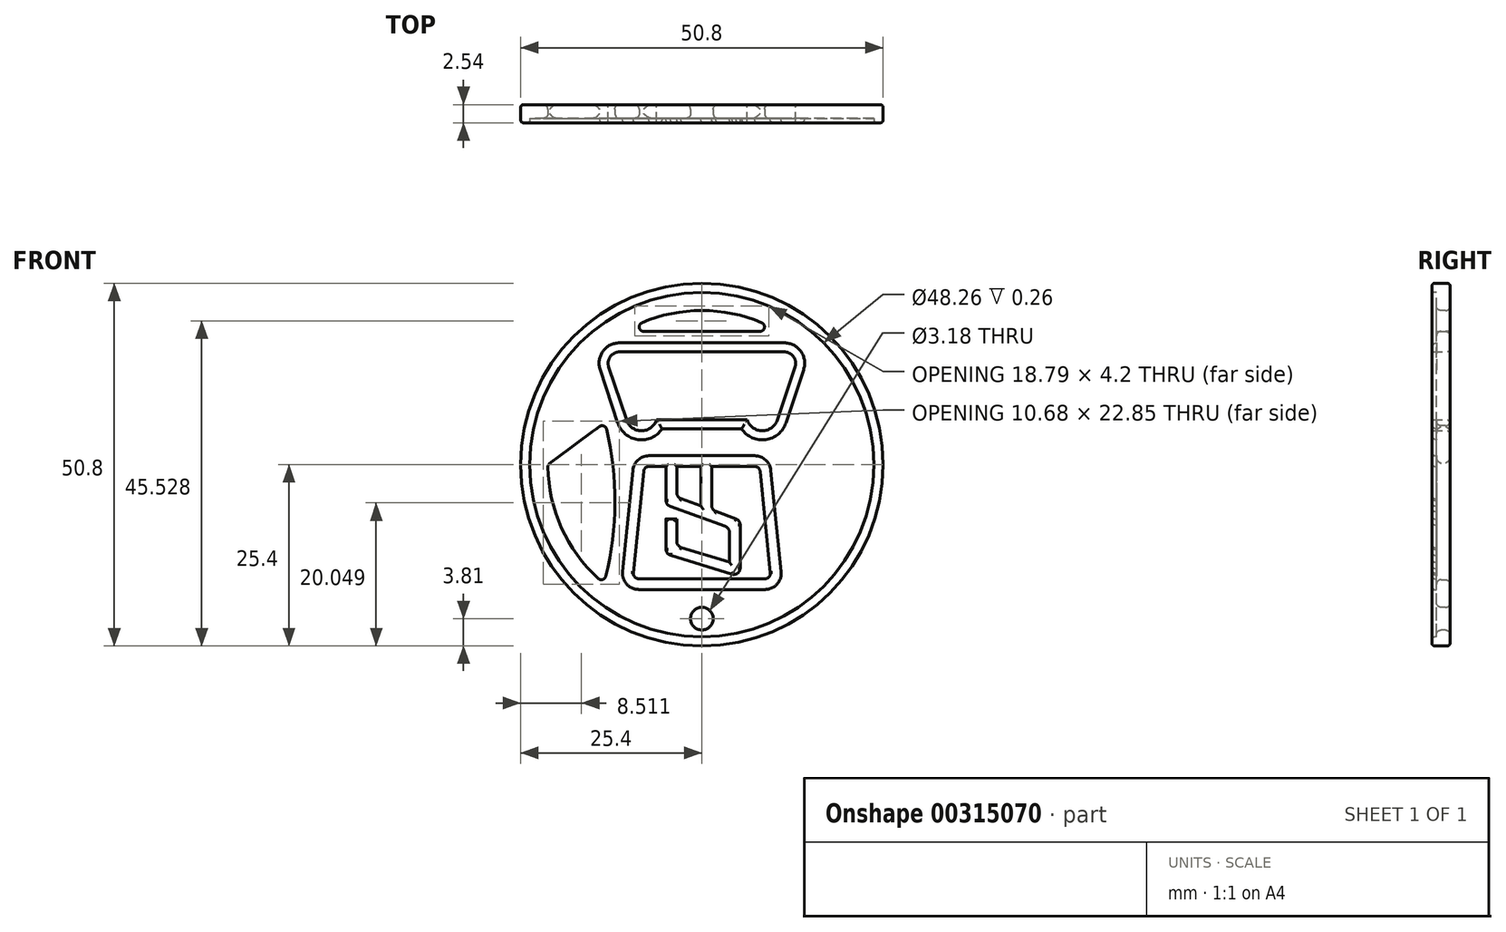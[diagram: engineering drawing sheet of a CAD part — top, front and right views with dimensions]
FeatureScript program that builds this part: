
annotation { "Feature Type Name" : "Feature", "Feature Type Description" : "" }
export const myFeature = defineFeature(function(context is Context, id is Id, definition is map)
    precondition{}
    {
        {
            var Q0;
            Q0=qCreatedBy(makeId("Front.planeOp"),FACE);
            var sketch = newSketch(context, id + "F0", { "sketchPlane" : qUnion([Q0])});
            skCircle(sketch, "E0", {"center": v(0, 0) * mm, "radius": 25.4 * mm});
            skLineSegment(sketch, "E1", {"start": v(0, 6.26) * mm, "end": v(6.35, 6.26) * mm});
            skArc(sketch, "E2", {"start": v(6.35, 6.26) * mm, "mid": v(8.47, 4.74) * mm, "end": v(10.58, 6.26) * mm});
            skLineSegment(sketch, "E3", {"start": v(10.58, 6.26) * mm, "end": v(13.06, 13.7) * mm});
            skLineSegment(sketch, "E4", {"start": v(11.55, 15.79) * mm, "end": v(0, 15.79) * mm});
            skLineSegment(sketch, "E5", {"start": v(0, 9.53) * mm, "end": v(0, 9.53) * mm});
            skLineSegment(sketch, "E6", {"start": v(0, 11.53) * mm, "end": v(0, 15.79) * mm, "construction": true});
            skPoint(sketch, "E7.visualSharp", {"position": v(13.76, 15.79) * mm});
            skArc(sketch, "E7.filletArc", {"start": v(13.06, 13.7) * mm, "mid": v(12.84, 15.13) * mm, "end": v(11.55, 15.79) * mm});
            skLineSegment(sketch, "E8.MirrorCS", {"start": v(0, 6.26) * mm, "end": v(-6.35, 6.26) * mm});
            skArc(sketch, "E9.MirrorCS", {"start": v(-6.35, 6.26) * mm, "mid": v(-8.47, 4.74) * mm, "end": v(-10.58, 6.26) * mm});
            skLineSegment(sketch, "E10.MirrorCS", {"start": v(-10.58, 6.26) * mm, "end": v(-13.06, 13.7) * mm});
            skPoint(sketch, "E11.MirrorP", {"position": v(-13.76, 15.79) * mm});
            skLineSegment(sketch, "E12.MirrorCS", {"start": v(-11.55, 15.79) * mm, "end": v(0, 15.79) * mm});
            skArc(sketch, "E13.MirrorCS", {"start": v(-13.06, 13.7) * mm, "mid": v(-12.84, 15.13) * mm, "end": v(-11.55, 15.79) * mm});
            skSolve(sketch);
        }
        {
            var Q0;
            Q0=makeQuery(id+"F0.imprint","IMPRINT",FACE,{"disambiguationData":[TD([[makeQuery(id+"F0.imprint","IMPRINT",EDGE,{"derivedFrom":sQuery(id+"F0.wireOp",EDGE,"E0")}),1.0]])]});
            var Q1;
            Q1=makeQuery(id+"F0.imprint","IMPRINT",FACE,{"disambiguationData":[TD([[makeQuery(id+"F0.imprint","IMPRINT",EDGE,{"derivedFrom":sQuery(id+"F0.wireOp",EDGE,"6BHQCYpu-HLr7-KWR4-XAYP-yZwnVEDkkDTz")}),1.0]])]});
            extrude(context, id + "F1", {"entities" : qUnion([Q0, Q1]), "endBound" : BoundingType.SYMMETRIC, "depth" : 2.54 * mm});
        }
        {
            var Q0;
            Q0=makeQuery(id+"F1.opExtrude","CAP_FACE",FACE,{"disambiguationData":[OSD([sQuery(id+"F0.wireOp",EDGE,"E0"),sQuery(id+"F0.wireOp",EDGE,"E1"),sQuery(id+"F0.wireOp",EDGE,"E2"),sQuery(id+"F0.wireOp",EDGE,"E3"),sQuery(id+"F0.wireOp",EDGE,"E4"),sQuery(id+"F0.wireOp",EDGE,"E7.filletArc"),sQuery(id+"F0.wireOp",EDGE,"E8.MirrorCS"),sQuery(id+"F0.wireOp",EDGE,"E9.MirrorCS"),sQuery(id+"F0.wireOp",EDGE,"E10.MirrorCS"),sQuery(id+"F0.wireOp",EDGE,"E12.MirrorCS"),sQuery(id+"F0.wireOp",EDGE,"E13.MirrorCS")])],"isStart":false});
            var sketch = newSketch(context, id + "F2", { "sketchPlane" : qUnion([Q0])});
            skCircle(sketch, "E14.0.0", {"center": v(0, 0) * mm, "radius": 25.4 * mm});
            skLineSegment(sketch, "E15", {"start": v(-11.55, 15.79) * mm, "end": v(11.55, 15.79) * mm});
            skArc(sketch, "E16", {"start": v(13.06, 13.7) * mm, "mid": v(12.84, 15.13) * mm, "end": v(11.55, 15.79) * mm});
            skLineSegment(sketch, "E17", {"start": v(10.58, 6.26) * mm, "end": v(13.06, 13.7) * mm});
            skArc(sketch, "E18", {"start": v(6.35, 6.26) * mm, "mid": v(8.47, 4.74) * mm, "end": v(10.58, 6.26) * mm});
            skLineSegment(sketch, "E19", {"start": v(-6.35, 6.26) * mm, "end": v(6.35, 6.26) * mm});
            skArc(sketch, "E20", {"start": v(-6.35, 6.26) * mm, "mid": v(-8.47, 4.74) * mm, "end": v(-10.58, 6.26) * mm});
            skLineSegment(sketch, "E21", {"start": v(-10.58, 6.26) * mm, "end": v(-13.06, 13.7) * mm});
            skArc(sketch, "E22", {"start": v(-13.06, 13.7) * mm, "mid": v(-12.84, 15.13) * mm, "end": v(-11.55, 15.79) * mm});
            skLineSegment(sketch, "E23.0", {"start": v(-5.58, 5) * mm, "end": v(5.58, 5) * mm});
            skArc(sketch, "E23.1", {"start": v(-5.58, 5) * mm, "mid": v(-8.95, 3.5) * mm, "end": v(-11.79, 5.86) * mm});
            skArc(sketch, "E23.2", {"start": v(5.58, 5) * mm, "mid": v(8.95, 3.5) * mm, "end": v(11.79, 5.86) * mm});
            skLineSegment(sketch, "E23.3", {"start": v(-11.79, 5.86) * mm, "end": v(-14.26, 13.3) * mm});
            skLineSegment(sketch, "E23.4", {"start": v(11.79, 5.86) * mm, "end": v(14.26, 13.3) * mm});
            skArc(sketch, "E23.5", {"start": v(14.26, 13.3) * mm, "mid": v(13.87, 15.87) * mm, "end": v(11.55, 17.06) * mm});
            skLineSegment(sketch, "E23.6", {"start": v(-11.55, 17.06) * mm, "end": v(11.55, 17.06) * mm});
            skArc(sketch, "E23.7", {"start": v(-14.26, 13.3) * mm, "mid": v(-13.87, 15.87) * mm, "end": v(-11.55, 17.06) * mm});
            skCircle(sketch, "E24.0", {"center": v(0, 0) * mm, "radius": 24.13 * mm});
            skSolve(sketch);
        }
        {
            var Q0;
            Q0=makeQuery(id+"F2.imprint","IMPRINT",FACE,{"disambiguationData":[TD([[makeQuery(id+"F2.imprint","IMPRINT",EDGE,{"derivedFrom":sQuery(id+"F2.wireOp",EDGE,"E23.0")}),-1.0]])]});
            extrude(context, id + "F3", {"entities" : qUnion([Q0]), "operationType" : NewBodyOperationType.REMOVE, "depth" : -0.64 * mm});
        }
        {
            var Q0;
            Q0=makeQuery(id+"F3.boolean.opBoolean","COPY",FACE,{"derivedFrom":makeQuery(id+"F3.opExtrude","CAP_FACE",FACE,{"disambiguationData":[OSD([sQuery(id+"F2.wireOp",EDGE,"E23.0"),sQuery(id+"F2.wireOp",EDGE,"E23.1"),sQuery(id+"F2.wireOp",EDGE,"E23.2"),sQuery(id+"F2.wireOp",EDGE,"E23.3"),sQuery(id+"F2.wireOp",EDGE,"E23.4"),sQuery(id+"F2.wireOp",EDGE,"E23.5"),sQuery(id+"F2.wireOp",EDGE,"E23.6"),sQuery(id+"F2.wireOp",EDGE,"E23.7"),sQuery(id+"F2.wireOp",EDGE,"E24.0")])],"isStart":false})});
            var sketch = newSketch(context, id + "F4", { "sketchPlane" : qUnion([Q0])});
            skCircle(sketch, "E25", {"center": v(0, -21.59) * mm, "radius": 1.59 * mm});
            skSolve(sketch);
        }
        {
            var Q0;
            Q0=makeQuery(id+"FFcqSu56bzkeG21_2.boolean.opBoolean","COPY",EDGE,{"derivedFrom":makeQuery(id+"FFcqSu56bzkeG21_2.opExtrude","CAP_EDGE",EDGE,{"disambiguationData":[OSD([sQuery(id+"F4.wireOp",EDGE,"E25")])],"isStart":true})});
            var Q1;
            Q1=makeQuery(id+"FFcqSu56bzkeG21_2.boolean.opBoolean","INTERSECT",EDGE,{"derivedFrom":[makeQuery(id+"FyMViEcAvyhJEX9_1.1.F3.boolean.opBoolean","COPY",FACE,{"derivedFrom":makeQuery(id+"FyMViEcAvyhJEX9_1.1.F3.opExtrude","CAP_FACE",FACE,{"disambiguationData":[OSD([sQuery(id+"F2.wireOp",EDGE,"E23.0"),sQuery(id+"F2.wireOp",EDGE,"E23.1"),sQuery(id+"F2.wireOp",EDGE,"E23.2"),sQuery(id+"F2.wireOp",EDGE,"E23.3"),sQuery(id+"F2.wireOp",EDGE,"E23.4"),sQuery(id+"F2.wireOp",EDGE,"E23.5"),sQuery(id+"F2.wireOp",EDGE,"E23.6"),sQuery(id+"F2.wireOp",EDGE,"E23.7"),sQuery(id+"F2.wireOp",EDGE,"E24.0")])],"isStart":false})}),makeQuery(id+"FFcqSu56bzkeG21_2.opExtrude","SWEPT_FACE",FACE,{"disambiguationData":[OSD([sQuery(id+"F4.wireOp",EDGE,"E25")])]})]});
            var Q2;
            {var subQ0=sQuery(id+"F0.wireOp",EDGE,"E0");Q2=makeQuery(id+"F3.boolean.opBoolean","SPLIT",FACE,{"disambiguationData":[TD([makeQuery(id+"F1.opExtrude","SWEPT_FACE",FACE,{"disambiguationData":[OSD([subQ0])]})])],"derivedFrom":makeQuery(id+"F1.opExtrude","CAP_FACE",FACE,{"disambiguationData":[OSD([subQ0,sQuery(id+"F0.wireOp",EDGE,"E1"),sQuery(id+"F0.wireOp",EDGE,"E2"),sQuery(id+"F0.wireOp",EDGE,"E3"),sQuery(id+"F0.wireOp",EDGE,"E4"),sQuery(id+"F0.wireOp",EDGE,"E7.filletArc"),sQuery(id+"F0.wireOp",EDGE,"E8.MirrorCS"),sQuery(id+"F0.wireOp",EDGE,"E9.MirrorCS"),sQuery(id+"F0.wireOp",EDGE,"E10.MirrorCS"),sQuery(id+"F0.wireOp",EDGE,"E12.MirrorCS"),sQuery(id+"F0.wireOp",EDGE,"E13.MirrorCS")])],"isStart":false})});}
            var Q3;
            {var subQ0=sQuery(id+"F0.wireOp",EDGE,"E0");Q3=makeQuery(id+"FyMViEcAvyhJEX9_1.1.F3.boolean.opBoolean","SPLIT",FACE,{"disambiguationData":[TD([makeQuery(id+"F1.opExtrude","SWEPT_FACE",FACE,{"disambiguationData":[OSD([subQ0])]})])],"derivedFrom":makeQuery(id+"F1.opExtrude","CAP_FACE",FACE,{"disambiguationData":[OSD([subQ0,sQuery(id+"F0.wireOp",EDGE,"E1"),sQuery(id+"F0.wireOp",EDGE,"E2"),sQuery(id+"F0.wireOp",EDGE,"E3"),sQuery(id+"F0.wireOp",EDGE,"E4"),sQuery(id+"F0.wireOp",EDGE,"E7.filletArc"),sQuery(id+"F0.wireOp",EDGE,"E8.MirrorCS"),sQuery(id+"F0.wireOp",EDGE,"E9.MirrorCS"),sQuery(id+"F0.wireOp",EDGE,"E10.MirrorCS"),sQuery(id+"F0.wireOp",EDGE,"E12.MirrorCS"),sQuery(id+"F0.wireOp",EDGE,"E13.MirrorCS")])],"isStart":true})});}
            fillet(context, id + "F5", {"entities" : qUnion([Q0, Q1, Q2, Q3]), "radius" : 0.38 * mm, "tangentPropagation" : true, "allowEdgeOverflow" : false});
        }
        {
            var Q0;
            Q0=makeQuery(id+"F4.imprint","IMPRINT",FACE,{"disambiguationData":[TD([[makeQuery(id+"F4.imprint","IMPRINT",EDGE,{"derivedFrom":sQuery(id+"F4.wireOp",EDGE,"E25")}),-1.0]])]});
            var sketch = newSketch(context, id + "F6", { "sketchPlane" : qUnion([Q0])});
            skLineSegment(sketch, "E26", {"start": v(-5.03, -0.27) * mm, "end": v(-7.42, -0.27) * mm});
            skLineSegment(sketch, "E27", {"start": v(-5.03, -0.27) * mm, "end": v(-5.03, -5) * mm});
            skArc(sketch, "E28", {"start": v(-5.03, -5) * mm, "mid": v(-4.87, -5.52) * mm, "end": v(-4.45, -5.84) * mm});
            skLineSegment(sketch, "E29", {"start": v(-4.45, -5.84) * mm, "end": v(3.27, -8.65) * mm});
            skArc(sketch, "E30", {"start": v(3.27, -8.65) * mm, "mid": v(3.7, -8.98) * mm, "end": v(3.86, -9.49) * mm});
            skLineSegment(sketch, "E31", {"start": v(3.86, -9.49) * mm, "end": v(3.86, -13.68) * mm});
            skLineSegment(sketch, "E32", {"start": v(3.86, -13.68) * mm, "end": v(-2.9, -11.6) * mm});
            skArc(sketch, "E33", {"start": v(-2.9, -11.6) * mm, "mid": v(-3.35, -11.27) * mm, "end": v(-3.52, -10.75) * mm});
            skLineSegment(sketch, "E34", {"start": v(-3.52, -10.75) * mm, "end": v(-3.52, -7.62) * mm});
            skLineSegment(sketch, "E35", {"start": v(-5.03, -7.62) * mm, "end": v(-3.52, -7.62) * mm});
            skLineSegment(sketch, "E36", {"start": v(-5.03, -11.86) * mm, "end": v(-5.03, -7.62) * mm});
            skArc(sketch, "E37", {"start": v(-5.03, -11.86) * mm, "mid": v(-4.86, -12.39) * mm, "end": v(-4.4, -12.71) * mm});
            skLineSegment(sketch, "E38", {"start": v(4.22, -15.37) * mm, "end": v(-4.4, -12.71) * mm});
            skArc(sketch, "E39", {"start": v(4.22, -15.37) * mm, "mid": v(5, -15.23) * mm, "end": v(5.37, -14.52) * mm});
            skLineSegment(sketch, "E40", {"start": v(5.37, -8.43) * mm, "end": v(5.37, -14.52) * mm});
            skArc(sketch, "E41", {"start": v(5.37, -8.43) * mm, "mid": v(5.2, -7.92) * mm, "end": v(4.79, -7.6) * mm});
            skLineSegment(sketch, "E42", {"start": v(1.96, -6.56) * mm, "end": v(4.79, -7.6) * mm});
            skArc(sketch, "E43", {"start": v(1.96, -6.56) * mm, "mid": v(1.53, -6.24) * mm, "end": v(1.37, -5.73) * mm});
            skLineSegment(sketch, "E44", {"start": v(1.37, -5.73) * mm, "end": v(1.37, -0.27) * mm});
            skLineSegment(sketch, "E45", {"start": v(7.42, -0.27) * mm, "end": v(1.37, -0.27) * mm});
            skArc(sketch, "E46", {"start": v(8.17, -0.94) * mm, "mid": v(7.93, -0.46) * mm, "end": v(7.42, -0.27) * mm});
            skLineSegment(sketch, "E47", {"start": v(9.6, -15.16) * mm, "end": v(8.17, -0.94) * mm});
            skArc(sketch, "E48", {"start": v(8.86, -15.99) * mm, "mid": v(9.42, -15.74) * mm, "end": v(9.6, -15.16) * mm});
            skLineSegment(sketch, "E49", {"start": v(-8.86, -15.99) * mm, "end": v(8.86, -15.99) * mm});
            skArc(sketch, "E50", {"start": v(-9.6, -15.16) * mm, "mid": v(-9.42, -15.74) * mm, "end": v(-8.86, -15.99) * mm});
            skLineSegment(sketch, "E51", {"start": v(-8.17, -0.94) * mm, "end": v(-9.6, -15.16) * mm});
            skArc(sketch, "E52", {"start": v(-7.42, -0.27) * mm, "mid": v(-7.93, -0.46) * mm, "end": v(-8.17, -0.94) * mm});
            skLineSegment(sketch, "E53", {"start": v(-3.52, -0.27) * mm, "end": v(-3.52, -3.95) * mm});
            skLineSegment(sketch, "E54", {"start": v(-0.14, -0.27) * mm, "end": v(-3.52, -0.27) * mm});
            skLineSegment(sketch, "E55", {"start": v(-0.14, -5.8) * mm, "end": v(-0.14, -0.27) * mm});
            skLineSegment(sketch, "E56", {"start": v(-2.93, -4.78) * mm, "end": v(-0.14, -5.8) * mm});
            skArc(sketch, "E57", {"start": v(-2.93, -4.78) * mm, "mid": v(-3.36, -4.46) * mm, "end": v(-3.52, -3.95) * mm});
            skLineSegment(sketch, "E58", {"start": v(-9.67, -0.8) * mm, "end": v(-11.11, -15) * mm});
            skArc(sketch, "E59", {"start": v(-11.11, -15) * mm, "mid": v(-10.54, -16.75) * mm, "end": v(-8.86, -17.5) * mm});
            skLineSegment(sketch, "E60", {"start": v(-8.86, -17.5) * mm, "end": v(8.86, -17.5) * mm});
            skArc(sketch, "E61", {"start": v(8.86, -17.5) * mm, "mid": v(10.54, -16.75) * mm, "end": v(11.11, -15) * mm});
            skLineSegment(sketch, "E62", {"start": v(11.11, -15) * mm, "end": v(9.67, -0.8) * mm});
            skArc(sketch, "E63", {"start": v(9.67, -0.8) * mm, "mid": v(8.94, 0.66) * mm, "end": v(7.42, 1.24) * mm});
            skLineSegment(sketch, "E64", {"start": v(7.42, 1.24) * mm, "end": v(-7.42, 1.24) * mm});
            skArc(sketch, "E65", {"start": v(-7.42, 1.24) * mm, "mid": v(-8.94, 0.66) * mm, "end": v(-9.67, -0.8) * mm});
            skSolve(sketch);
        }
        {
            var Q0;
            Q0=makeQuery(id+"F6.imprint","IMPRINT",FACE,{"disambiguationData":[TD([[makeQuery(id+"F6.imprint","IMPRINT",EDGE,{"derivedFrom":sQuery(id+"F6.wireOp",EDGE,"E26")}),-1.0]])]});
            var Q1;
            {var subQ0=sQuery(id+"F0.wireOp",EDGE,"E2");var subQ1=sQuery(id+"F0.wireOp",EDGE,"E13.MirrorCS");var subQ2=sQuery(id+"F0.wireOp",EDGE,"E10.MirrorCS");var subQ3=sQuery(id+"F0.wireOp",EDGE,"E9.MirrorCS");var subQ4=sQuery(id+"F0.wireOp",EDGE,"E7.filletArc");var subQ5=sQuery(id+"F0.wireOp",EDGE,"E8.MirrorCS");var subQ6=sQuery(id+"F0.wireOp",EDGE,"E1");var subQ7=sQuery(id+"F0.wireOp",EDGE,"E3");var subQ8=sQuery(id+"F0.wireOp",EDGE,"E12.MirrorCS");var subQ9=sQuery(id+"F0.wireOp",EDGE,"E4");Q1=makeQuery(id+"F3.boolean.opBoolean","SPLIT",FACE,{"disambiguationData":[TD([makeQuery(id+"F1.opExtrude","SWEPT_FACE",FACE,{"disambiguationData":[OSD([subQ0])]})])],"derivedFrom":makeQuery(id+"F1.opExtrude","CAP_FACE",FACE,{"disambiguationData":[OSD([sQuery(id+"F0.wireOp",EDGE,"E0"),subQ6,subQ0,subQ7,subQ9,subQ4,subQ5,subQ3,subQ2,subQ8,subQ1])],"isStart":false})});}
            extrude(context, id + "F7", {"entities" : qUnion([Q0]), "operationType" : NewBodyOperationType.ADD, "endBound" : BoundingType.UP_TO_SURFACE, "endBoundEntityFace" : qUnion([Q1]), "depth" : 1.59 * mm});
        }
        {
            var Q0;
            Q0=makeQuery(id+"F4.imprint","IMPRINT",FACE,{"disambiguationData":[TD([[makeQuery(id+"F4.imprint","IMPRINT",EDGE,{"derivedFrom":sQuery(id+"F4.wireOp",EDGE,"E25")}),1.0]])]});
            extrude(context, id + "F8", {"entities" : qUnion([Q0]), "operationType" : NewBodyOperationType.REMOVE, "oppositeDirection" : true, "depth" : 2.54 * mm});
        }
        {
            var Q0;
            Q0=makeQuery(id+"F8.boolean.opBoolean","COPY",FACE,{"derivedFrom":makeQuery(id+"F8.opExtrude","SWEPT_FACE",FACE,{"disambiguationData":[OSD([sQuery(id+"F4.wireOp",EDGE,"E25")])]})});
            fillet(context, id + "F9", {"entities" : qUnion([Q0]), "radius" : 0.64 * mm, "tangentPropagation" : true, "allowEdgeOverflow" : false});
        }
        {
            var Q0;
            {var subQ0=sQuery(id+"F2.wireOp",EDGE,"E24.0");var subQ1=sQuery(id+"F2.wireOp",EDGE,"E23.7");var subQ2=sQuery(id+"F2.wireOp",EDGE,"E23.6");var subQ3=sQuery(id+"F2.wireOp",EDGE,"E23.5");var subQ4=sQuery(id+"F2.wireOp",EDGE,"E23.4");var subQ5=sQuery(id+"F2.wireOp",EDGE,"E23.0");var subQ6=sQuery(id+"F2.wireOp",EDGE,"E23.1");var subQ7=sQuery(id+"F2.wireOp",EDGE,"E23.2");var subQ8=sQuery(id+"F2.wireOp",EDGE,"E23.3");Q0=makeQuery(id+"F7.boolean.opBoolean","SPLIT",FACE,{"disambiguationData":[TD([makeQuery(id+"F3.boolean.opBoolean","COPY",FACE,{"derivedFrom":makeQuery(id+"F3.opExtrude","SWEPT_FACE",FACE,{"disambiguationData":[OSD([subQ5])]})})])],"derivedFrom":makeQuery(id+"F3.boolean.opBoolean","COPY",FACE,{"derivedFrom":makeQuery(id+"F3.opExtrude","CAP_FACE",FACE,{"disambiguationData":[OSD([subQ5,subQ6,subQ7,subQ8,subQ4,subQ3,subQ2,subQ1,subQ0])],"isStart":false})})});}
            var sketch = newSketch(context, id + "F10", { "sketchPlane" : qUnion([Q0])});
            skCircle(sketch, "E66.0", {"center": v(0, 0) * mm, "radius": 24.13 * mm});
            skCircle(sketch, "E67.0", {"center": v(0, 0) * mm, "radius": 21.59 * mm});
            skArc(sketch, "E68", {"start": v(-13.74, -16.66) * mm, "mid": v(-12.37, -1.12) * mm, "end": v(-16.51, 13.91) * mm});
            skArc(sketch, "E69.MirrorCS", {"start": v(13.74, -16.66) * mm, "mid": v(12.37, -1.12) * mm, "end": v(16.51, 13.91) * mm});
            skLineSegment(sketch, "E70", {"start": v(-21.59, 0) * mm, "end": v(-13.58, 5.9) * mm});
            skLineSegment(sketch, "E71", {"start": v(-21.59, 0) * mm, "end": v(-17.97, 0) * mm, "construction": true});
            skLineSegment(sketch, "E72.MirrorCS", {"start": v(-21.59, 0) * mm, "end": v(-12.22, -6.9) * mm});
            skPoint(sketch, "E73.orphan", {"position": v(-13.58, -5.9) * mm});
            skLineSegment(sketch, "E74", {"start": v(-10.86, 18.66) * mm, "end": v(10.86, 18.66) * mm});
            skSolve(sketch);
        }
        {
            var Q0;
            {var subQ0=sQuery(id+"F10.wireOp",EDGE,"E68");Q0=makeQuery(id+"F10.imprint","IMPRINT",FACE,{"disambiguationData":[TD([[makeQuery(id+"F10.imprint","IMPRINT",EDGE,{"derivedFrom":subQ0}),1.0]])]});}
            var Q1;
            {var subQ0=sQuery(id+"F10.wireOp",EDGE,"E69.MirrorCS");Q1=makeQuery(id+"F10.imprint","IMPRINT",FACE,{"disambiguationData":[TD([[makeQuery(id+"F10.imprint","IMPRINT",EDGE,{"derivedFrom":subQ0}),-1.0]])]});}
            extrude(context, id + "F11", {"entities" : qUnion([Q0, Q1]), "operationType" : NewBodyOperationType.REMOVE, "endBound" : BoundingType.UP_TO_NEXT, "oppositeDirection" : true, "depth" : 25.4 * mm});
        }
        {
            var Q0;
            Q0=makeQuery(id+"F3.boolean.opBoolean","COPY",EDGE,{"derivedFrom":makeQuery(id+"F3.opExtrude","CAP_EDGE",EDGE,{"disambiguationData":[OSD([sQuery(id+"F2.wireOp",EDGE,"E23.6")])],"isStart":true})});
            var Q1;
            Q1=makeQuery(id+"F3.boolean.opBoolean","COPY",EDGE,{"derivedFrom":makeQuery(id+"F3.opExtrude","CAP_EDGE",EDGE,{"disambiguationData":[OSD([sQuery(id+"F2.wireOp",EDGE,"E23.0")])],"isStart":true})});
            var Q2;
            Q2=makeQuery(id+"FyMViEcAvyhJEX9_1.1.F3.boolean.opBoolean","COPY",EDGE,{"derivedFrom":makeQuery(id+"FyMViEcAvyhJEX9_1.1.F3.opExtrude","CAP_EDGE",EDGE,{"disambiguationData":[OSD([sQuery(id+"F2.wireOp",EDGE,"E23.6")])],"isStart":true})});
            var Q3;
            {var subQ0=sQuery(id+"F10.wireOp",EDGE,"E69.MirrorCS");var subQ1=sQuery(id+"F10.wireOp",EDGE,"E67.0");Q3=makeQuery(id+"F11.boolean.opBoolean","COPY",FACE,{"derivedFrom":makeQuery(id+"F11.opExtrude","SWEPT_FACE",FACE,{"disambiguationData":[OSD([subQ1]),TDD([makeQuery(id+"F10.imprint","IMPRINT",EDGE,{"disambiguationData":[TD([[makeQuery(id+"F10.imprint","INTERSECT",VERTEX,{"disambiguationData":[OD(0.0)],"derivedFrom":[subQ1,subQ0]}),-1.0]])],"derivedFrom":subQ1})])]})});}
            var Q4;
            Q4=makeQuery(id+"F11.boolean.opBoolean","COPY",FACE,{"derivedFrom":makeQuery(id+"F11.opExtrude","SWEPT_FACE",FACE,{"disambiguationData":[OSD([sQuery(id+"F10.wireOp",EDGE,"E69.MirrorCS")])]})});
            var Q5;
            Q5=makeQuery(id+"F11.boolean.opBoolean","COPY",FACE,{"derivedFrom":makeQuery(id+"F11.opExtrude","SWEPT_FACE",FACE,{"disambiguationData":[OSD([sQuery(id+"F10.wireOp",EDGE,"E68")])]})});
            var Q6;
            {var subQ0=sQuery(id+"F10.wireOp",EDGE,"E68");var subQ1=sQuery(id+"F10.wireOp",EDGE,"E67.0");Q6=makeQuery(id+"F11.boolean.opBoolean","COPY",EDGE,{"derivedFrom":makeQuery(id+"F11.opExtrude","TWEAK_EDGE",EDGE,{"derivedFrom":[makeQuery(id+"FyMViEcAvyhJEX9_1.1.F3.boolean.opBoolean","COPY",FACE,{"derivedFrom":makeQuery(id+"FyMViEcAvyhJEX9_1.1.F3.opExtrude","CAP_FACE",FACE,{"disambiguationData":[OSD([sQuery(id+"F2.wireOp",EDGE,"E23.0"),sQuery(id+"F2.wireOp",EDGE,"E23.1"),sQuery(id+"F2.wireOp",EDGE,"E23.2"),sQuery(id+"F2.wireOp",EDGE,"E23.3"),sQuery(id+"F2.wireOp",EDGE,"E23.4"),sQuery(id+"F2.wireOp",EDGE,"E23.5"),sQuery(id+"F2.wireOp",EDGE,"E23.6"),sQuery(id+"F2.wireOp",EDGE,"E23.7"),sQuery(id+"F2.wireOp",EDGE,"E24.0")])],"isStart":false})}),makeQuery(id+"F10.imprint","IMPRINT",EDGE,{"disambiguationData":[TD([[makeQuery(id+"F10.imprint","INTERSECT",VERTEX,{"disambiguationData":[OD(0.0)],"derivedFrom":[subQ1,subQ0]}),1.0]])],"derivedFrom":subQ1})]})});}
            var Q7;
            {var subQ0=sQuery(id+"F10.wireOp",EDGE,"E68");var subQ1=sQuery(id+"F10.wireOp",EDGE,"E67.0");Q7=makeQuery(id+"F11.boolean.opBoolean","COPY",FACE,{"derivedFrom":makeQuery(id+"F11.opExtrude","SWEPT_FACE",FACE,{"disambiguationData":[OSD([subQ1]),TDD([makeQuery(id+"F10.imprint","IMPRINT",EDGE,{"disambiguationData":[TD([[makeQuery(id+"F10.imprint","INTERSECT",VERTEX,{"disambiguationData":[OD(0.0)],"derivedFrom":[subQ1,subQ0]}),1.0]])],"derivedFrom":subQ1})])]})});}
            var Q8;
            Q8=makeQuery(id+"FyMViEcAvyhJEX9_1.1.F3.boolean.opBoolean","COPY",EDGE,{"derivedFrom":makeQuery(id+"FyMViEcAvyhJEX9_1.1.F3.opExtrude","CAP_EDGE",EDGE,{"disambiguationData":[OSD([sQuery(id+"F2.wireOp",EDGE,"E23.0")])],"isStart":true})});
            fillet(context, id + "F12", {"entities" : qUnion([Q0, Q1, Q2, Q3, Q4, Q5, Q6, Q7, Q8]), "radius" : 0.64 * mm, "tangentPropagation" : true, "allowEdgeOverflow" : false});
        }
        {
            var Q0;
            Q0=makeQuery(id+"F7.opExtrude","CAP_FACE",FACE,{"disambiguationData":[OSD([sQuery(id+"F6.wireOp",EDGE,"E26"),sQuery(id+"F6.wireOp",EDGE,"E27"),sQuery(id+"F6.wireOp",EDGE,"E28"),sQuery(id+"F6.wireOp",EDGE,"E29"),sQuery(id+"F6.wireOp",EDGE,"E30"),sQuery(id+"F6.wireOp",EDGE,"E31"),sQuery(id+"F6.wireOp",EDGE,"E32"),sQuery(id+"F6.wireOp",EDGE,"E33"),sQuery(id+"F6.wireOp",EDGE,"E34"),sQuery(id+"F6.wireOp",EDGE,"E35"),sQuery(id+"F6.wireOp",EDGE,"E36"),sQuery(id+"F6.wireOp",EDGE,"E37"),sQuery(id+"F6.wireOp",EDGE,"E38"),sQuery(id+"F6.wireOp",EDGE,"E39"),sQuery(id+"F6.wireOp",EDGE,"E40"),sQuery(id+"F6.wireOp",EDGE,"E41"),sQuery(id+"F6.wireOp",EDGE,"E42"),sQuery(id+"F6.wireOp",EDGE,"E43"),sQuery(id+"F6.wireOp",EDGE,"E44"),sQuery(id+"F6.wireOp",EDGE,"E45"),sQuery(id+"F6.wireOp",EDGE,"E46"),sQuery(id+"F6.wireOp",EDGE,"E47"),sQuery(id+"F6.wireOp",EDGE,"E48"),sQuery(id+"F6.wireOp",EDGE,"E49"),sQuery(id+"F6.wireOp",EDGE,"E50"),sQuery(id+"F6.wireOp",EDGE,"E51"),sQuery(id+"F6.wireOp",EDGE,"E52"),sQuery(id+"F6.wireOp",EDGE,"E53"),sQuery(id+"F6.wireOp",EDGE,"E54"),sQuery(id+"F6.wireOp",EDGE,"E55"),sQuery(id+"F6.wireOp",EDGE,"E56"),sQuery(id+"F6.wireOp",EDGE,"E57"),sQuery(id+"F6.wireOp",EDGE,"E58"),sQuery(id+"F6.wireOp",EDGE,"E59"),sQuery(id+"F6.wireOp",EDGE,"E60"),sQuery(id+"F6.wireOp",EDGE,"E61"),sQuery(id+"F6.wireOp",EDGE,"E62"),sQuery(id+"F6.wireOp",EDGE,"E63"),sQuery(id+"F6.wireOp",EDGE,"E64"),sQuery(id+"F6.wireOp",EDGE,"E65")])],"isStart":false});
            fillet(context, id + "F13", {"entities" : qUnion([Q0]), "radius" : 0.32 * mm, "tangentPropagation" : true, "allowEdgeOverflow" : false});
        }
        {
            var Q0;
            {var subQ0=sQuery(id+"F10.wireOp",EDGE,"E74");Q0=makeQuery(id+"F10.imprint","IMPRINT",FACE,{"disambiguationData":[TD([[makeQuery(id+"F10.imprint","IMPRINT",EDGE,{"derivedFrom":subQ0}),1.0]])]});}
            extrude(context, id + "F14", {"entities" : qUnion([Q0]), "operationType" : NewBodyOperationType.REMOVE, "endBound" : BoundingType.UP_TO_NEXT, "oppositeDirection" : true, "depth" : 25.4 * mm});
        }
        {
            var Q0;
            Q0=makeQuery(id+"F14.boolean.opBoolean","COPY",FACE,{"derivedFrom":makeQuery(id+"F14.opExtrude","SWEPT_FACE",FACE,{"disambiguationData":[OSD([sQuery(id+"F10.wireOp",EDGE,"E67.0")])]})});
            fillet(context, id + "F15", {"entities" : qUnion([Q0]), "radius" : 0.64 * mm, "tangentPropagation" : true, "allowEdgeOverflow" : false});
        }
    });
